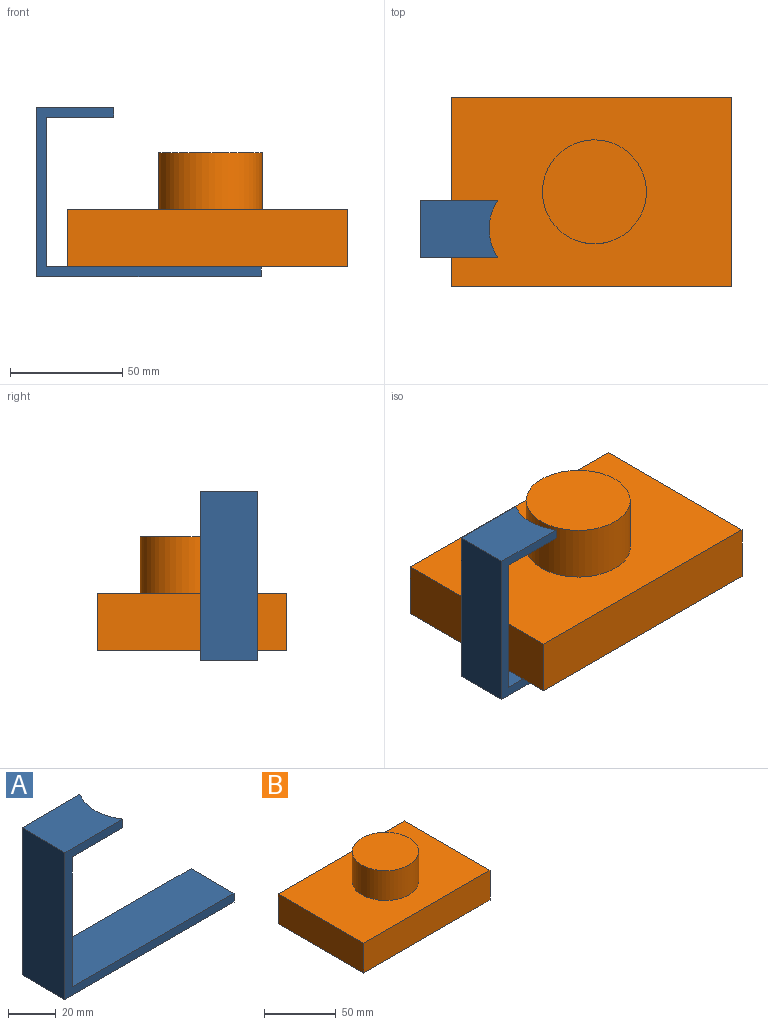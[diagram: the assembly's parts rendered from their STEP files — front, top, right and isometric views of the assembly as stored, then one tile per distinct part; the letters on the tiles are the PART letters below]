
ASSEMBLY  parts=2 mates=1
PART A: 10 faces, bbox 99.9x25.4x75.3 mm
  f0: plane 75.3x25.4mm, normal (-1,0,0), area 1912.7mm2, adj f1,f5,f6,f8
  f1: plane 99.94x25.4mm, normal (0,0,-1), area 2538.4mm2, adj f0,f2,f5,f6
  f2: plane 25.4x4.41mm, normal (1,0,0), area 111.9mm2, adj f1,f3,f5,f6
  f3: plane 95.53x25.4mm, normal (0,0,1), area 2426.5mm2, adj f2,f4,f5,f6
  f4: plane 66.49x25.4mm, normal (1,0,0), area 1688.9mm2, adj f3,f5,f6,f7
  f5: plane 99.94x75.3mm, normal (0,1,0), area 884.2mm2, adj f0,f1,f2,f3,f4,f7,f8,f9
  f6: plane 99.94x75.3mm, normal (0,-1,0), area 884.2mm2, adj f0,f1,f2,f3,f4,f7,f8,f9
  f7: plane 29.85x25.4mm, normal (0,0,-1), area 692.7mm2, adj f4,f5,f6,f9
  f8: plane 34.26x25.4mm, normal (0,0,1), area 804.6mm2, adj f0,f5,f6,f9
  f9: cylinder r=23.12mm len=25.4mm, axis (0,0,1), area 118.5mm2, adj f5,f6,f7,f8
PART B: 8 faces, bbox 124.6x84.3x50.8 mm
  f0: plane 124.59x25.4mm, normal (0,-1,0), area 3164.6mm2, adj f1,f3,f4,f5
  f1: plane 84.26x25.4mm, normal (1,0,0), area 2140.1mm2, adj f0,f2,f4,f5
  f2: plane 124.59x25.4mm, normal (0,1,0), area 3164.6mm2, adj f1,f3,f4,f5
  f3: plane 84.26x25.4mm, normal (-1,0,0), area 2140.1mm2, adj f0,f2,f4,f5
  f4: plane 124.59x84.26mm, normal (0,0,1), area 8818.3mm2, adj f0,f1,f2,f3,f6
  f5: plane 124.59x84.26mm, normal (0,0,-1), area 10497.3mm2, adj f0,f1,f2,f3
  f6: cylinder r=23.12mm len=46.24mm, axis (0,0,-1), area 3689.6mm2, adj f4,f7
  f7: plane 46.24x46.24mm, normal (0,0,1), area 1679.1mm2, adj f6
PLACE A t=(-30.36,-4.02,-9.15)mm
PLACE B t=(0.84,-0.19,-42.4)mm
MATE planar A.f3 <-> B.f5  axis (0,0,1) through (-22.85,-16.72,-42.4)mm
